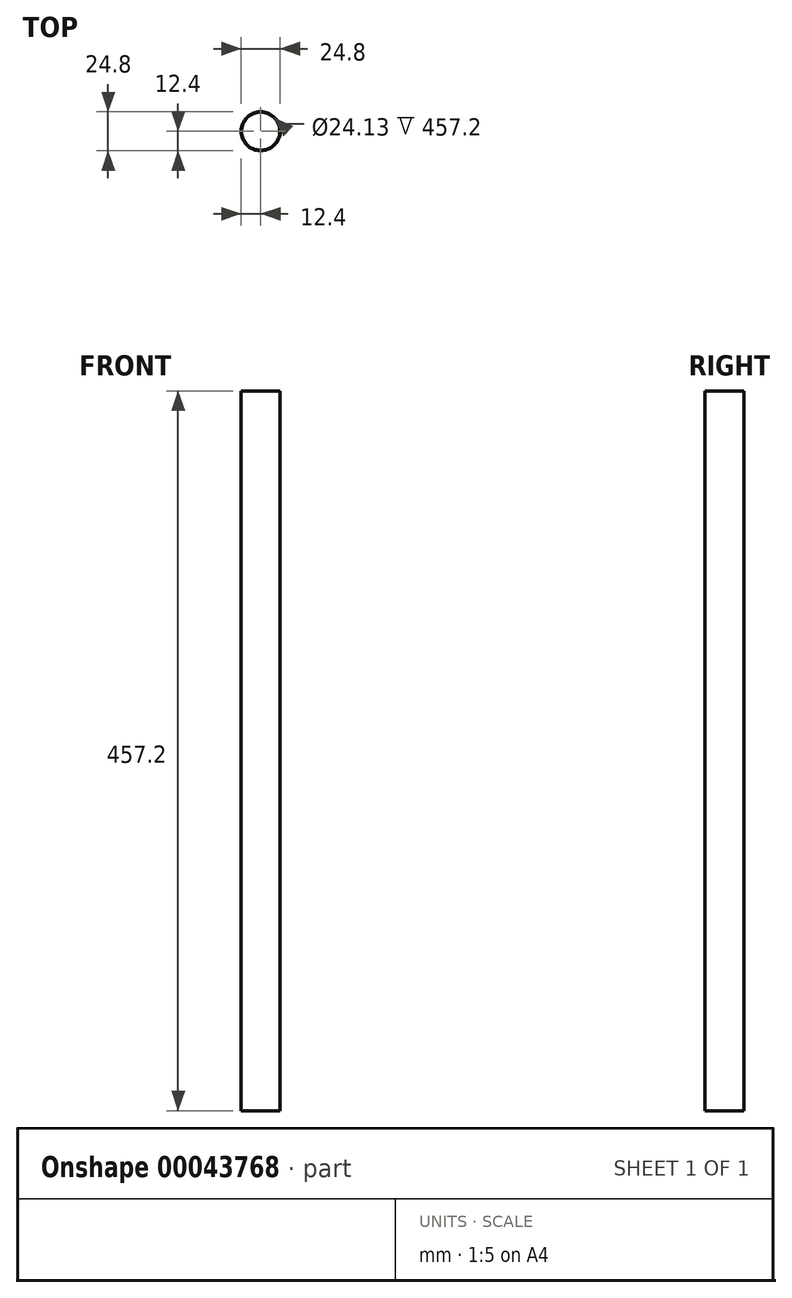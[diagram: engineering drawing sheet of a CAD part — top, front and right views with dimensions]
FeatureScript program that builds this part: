
annotation { "Feature Type Name" : "Feature", "Feature Type Description" : "" }
export const myFeature = defineFeature(function(context is Context, id is Id, definition is map)
    precondition{}
    {
        {
            var Q0;
            Q0=qCreatedBy(makeId("Front.planeOp"),FACE);
            var sketch = newSketch(context, id + "F0", { "sketchPlane" : qUnion([Q0])});
            skLineSegment(sketch, "E0", {"start": v(0, 0) * mm, "end": v(12.07, 0) * mm});
            skLineSegment(sketch, "E1", {"start": v(12.07, 0) * mm, "end": v(12.07, 457.2) * mm});
            skLineSegment(sketch, "E2", {"start": v(12.06, 457.2) * mm, "end": v(12.4, 457.2) * mm});
            skLineSegment(sketch, "E3", {"start": v(12.4, 457.2) * mm, "end": v(12.4, 0) * mm});
            skLineSegment(sketch, "E4", {"start": v(12.4, 0) * mm, "end": v(12.07, 0) * mm});
            skLineSegment(sketch, "E5", {"start": v(0, 0) * mm, "end": v(0, 457.2) * mm});
            skLineSegment(sketch, "E6", {"start": v(0, 457.2) * mm, "end": v(12.06, 457.2) * mm});
            skSolve(sketch);
        }
        {
            var Q0;
            Q0=makeQuery(id+"F0.imprint","IMPRINT",FACE,{"disambiguationData":[TD([[makeQuery(id+"F0.imprint","IMPRINT",EDGE,{"derivedFrom":sQuery(id+"F0.wireOp",EDGE,"E1")}),-1.0]])]});
            var Q1;
            Q1=sQuery(id+"F0.wireOp",EDGE,"E5");
            revolve(context, id + "F1", {"entities" : qUnion([Q0]), "axis" : qUnion([Q1]), "revolveType" : RevolveType.FULL});
        }
        {
            var Q0;
            Q0=qCreatedBy(makeId("Top.planeOp"),FACE);
            var sketch = newSketch(context, id + "F2", { "sketchPlane" : qUnion([Q0])});
            skCircle(sketch, "E7.0", {"center": v(0, 0) * mm, "radius": 12.4 * mm});
            skLineSegment(sketch, "E8", {"start": v(0, 0) * mm, "end": v(0, 12.4) * mm});
            skLineSegment(sketch, "E9", {"start": v(0, 0) * mm, "end": v(0, -12.4) * mm});
            skLineSegment(sketch, "E10", {"start": v(0, 0) * mm, "end": v(10.73, -6.2) * mm});
            skLineSegment(sketch, "E11.MirrorCS", {"start": v(0, 0) * mm, "end": v(-10.73, -6.2) * mm});
            skSolve(sketch);
        }
    });
